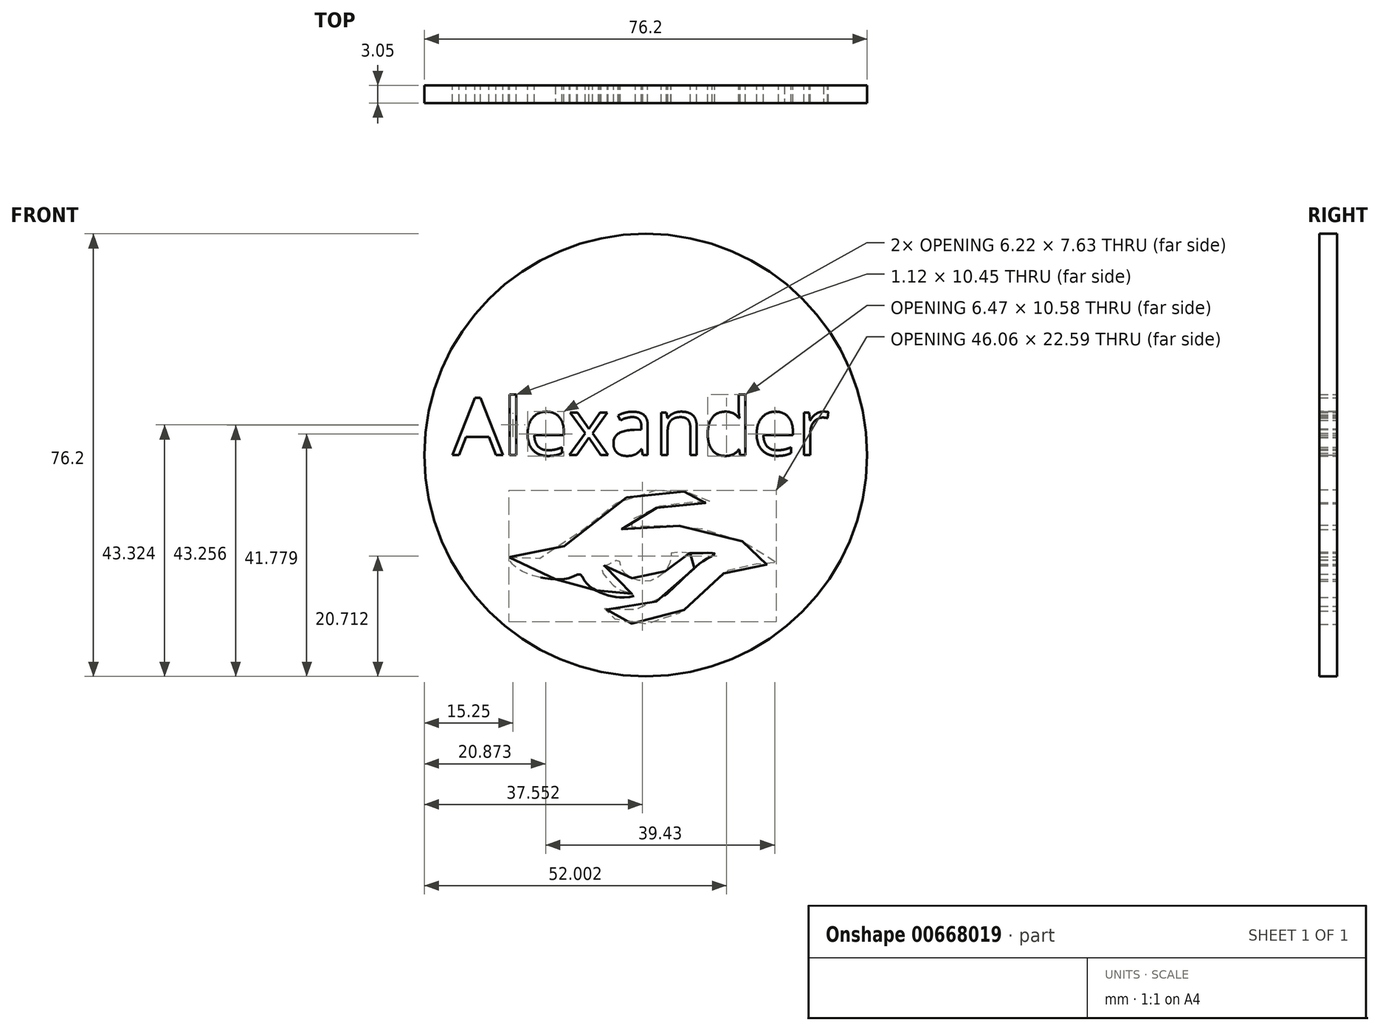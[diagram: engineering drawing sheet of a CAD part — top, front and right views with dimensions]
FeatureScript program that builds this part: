
annotation { "Feature Type Name" : "Feature", "Feature Type Description" : "" }
export const myFeature = defineFeature(function(context is Context, id is Id, definition is map)
    precondition{}
    {
        {
            var Q0;
            Q0=qCreatedBy(makeId("Front.planeOp"),FACE);
            var sketch = newSketch(context, id + "F0", { "sketchPlane" : qUnion([Q0])});
            skCircle(sketch, "E0", {"center": v(0, 0) * mm, "radius": 38.1 * mm});
            skText(sketch, "E1", { "text": "Alexander\n", "fontName": "OpenSans-Regular.ttf"});
            skFitSpline(sketch, "E2", {"points": [v(-23.58, -17.6) * mm, v(-21.37, -17.91) * mm, v(-18.8, -17.81) * mm, v(-15.86, -16.9) * mm, v(-8.84, -11.04) * mm, v(-6.31, -9.02) * mm, v(-1.96, -6.74) * mm, v(1.57, -6.03) * mm, v(3.55, -5.93) * mm, v(6.73, -6.29) * mm, v(8.35, -6.64) * mm, v(9.67, -7.13) * mm, v(10.77, -7.75) * mm, v(11.45, -8.28) * mm, v(9.86, -8.2) * mm, v(7.64, -8.16) * mm, v(5.37, -8.26) * mm, v(3.28, -8.54) * mm, v(1.07, -9.37) * mm, v(-1.1, -10.28) * mm, v(-3.08, -11.55) * mm, v(-4.61, -12.76) * mm, v(-2.71, -12.39) * mm, v(0, -12.05) * mm, v(3.44, -12.05) * mm, v(6.53, -12.2) * mm, v(9.76, -12.66) * mm, v(14.41, -13.92) * mm, v(17.95, -15.49) * mm, v(21.29, -17.5) * mm, v(22.83, -18.93) * mm, v(20.88, -18.82) * mm, v(19.16, -18.77) * mm, v(17.34, -18.77) * mm, v(15.12, -19.38) * mm, v(13.55, -20.24) * mm, v(11.94, -21.55) * mm, v(10.12, -23.47) * mm, v(7.8, -25.65) * mm, v(5.67, -27.26) * mm, v(2.99, -28.48) * mm, v(0, -29.08) * mm, v(-2.62, -28.93) * mm, v(-4.9, -28.38) * mm, v(-7.52, -26.96) * mm, v(-8.13, -26) * mm, v(-6.46, -26.66) * mm, v(-4.29, -26.8) * mm, v(-1.71, -26.56) * mm, v(0.72, -25.8) * mm, v(2.84, -24.48) * mm, v(4.46, -23.12) * mm, v(6.48, -21.2) * mm, v(8.1, -19.68) * mm, v(10.27, -17.96) * mm, v(11.89, -16.95) * mm, v(9.91, -16.85) * mm, v(7.19, -16.8) * mm, v(4.4, -16.84) * mm, v(4.35, -17.3) * mm, v(4.3, -18.06) * mm, v(3.95, -18.87) * mm, v(3.55, -19.73) * mm, v(2.69, -20.6) * mm, v(1.32, -21.45) * mm, v(0, -21.7) * mm, v(-0.9, -21.6) * mm, v(-1.96, -21.35) * mm, v(-3.38, -20.54) * mm, v(-4.19, -19.63) * mm, v(-4.54, -18.17) * mm, v(-4.9, -18.07) * mm, v(-6.56, -18.87) * mm, v(-7.67, -19.36) * mm, v(-6.92, -20.95) * mm, v(-5.83, -22.14) * mm, v(-4.29, -23.27) * mm, v(-1.79, -24.1) * mm, v(-3.68, -24.48) * mm, v(-5.55, -24.33) * mm, v(-7.42, -23.83) * mm, v(-9.2, -22.87) * mm, v(-10.43, -21.75) * mm, v(-11.3, -20.54) * mm, v(-13.34, -21.2) * mm, v(-17.28, -21.2) * mm, v(-19.55, -20.7) * mm, v(-22.49, -19.18) * mm, v(-23.58, -17.6) * mm]});
            const initialGuessF0  = {"E1": [-0.03329, 0, 1, 0, 0.0099]};
            skSetInitialGuess(sketch, initialGuessF0);
            skSolve(sketch);
        }
        {
            var Q0;
            Q0=makeQuery(id+"F0.imprint","IMPRINT",FACE,{"disambiguationData":[TD([[makeQuery(id+"F0.imprint","IMPRINT",EDGE,{"derivedFrom":sQuery(id+"F0.wireOp",EDGE,"E0")}),1.0]])]});
            extrude(context, id + "F1", {"entities" : qUnion([Q0]), "depth" : 3.05 * mm, "offsetDistance" : 25.4 * mm});
        }
    });
